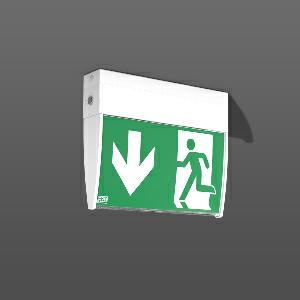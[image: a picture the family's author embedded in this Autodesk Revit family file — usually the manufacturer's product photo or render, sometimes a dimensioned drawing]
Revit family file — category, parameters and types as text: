
# Revit family: gsun_d_672219_002_1_04_1060
name_source: partatom
category: Lighting Fixtures
units: mm (PartAtom-declared; Revit-internal decimal feet)

## family parameters
Cut with Voids When Loaded = No
Host = Face
Light Source = No
Part Type = Normal
Room Calculation Point = No
Round Connector Dimension = Use Diameter
Shared = No

## types (1)
- GSUN D
    Apparent Load = 0 VA
    Default Elevation = 1800 mm
    Description = Series: GSUN D
Luminaire for escape route identification. Housing: extruded aluminium profile, powder-coated. 4 legends and 1 white lay in plastic sheet included. Universal mounting kit for ceiling and wall surface mounting. Electronic ballast included. Self-contained system with automatic self-test and feedback to the RZB monitoring system MULTIDIGIT. 
Colour: white
Length: 247 mm
Width: 45 mm
Height: 200 mm
Weight: 0.9 kg
Operating mode: maintained power mode
Viewing Distance: 24 m
Duration time: 3 h
Lamp: LED
Socket: without socket
Colour temperature: 4000K
System power: 4.7 W
Control gear: Regulated power supply
Protection class: I
Type of protection: IP 30
    Height = 200 mm  [stored 0.656168 ft]
    Lamp = 0 x
    Length = 247 mm
    Luminous efficacy = 0 lm/W
    Manufacturer = RZB
    ModVariant = No
    Model = 672219.002.1.04
    Mounting Place = Ceiling, Wall
    Mounting Type = Surface mounted
    Number of Poles = 1
    OnlyDefault = Yes
    Power Factor = 1
    Product Name = GSUN D
    Product group = Surface mounted ceiling and wall luminaires
    ProductGroupID = 305
    Protection Class = Protection class I
    Protection Degree = IP 30
    RLX_Detail_Level = 1
    RLX_Emergency_Light_Flux = 0 lm
    RLX_Emergency_Type = 0
    RLX_Emergency_Type_DB = No
    RlxData = <blob elided: 30085 chars, md5=b2e42442>
    Standby Power = 0 W
    System Light Flux = 0 lm
    System Power = 0 W
    Type Comments = Product without accessories
    Type Image = 671995.002.1.jpg
    URL = http://relux.com
    VarID = ---
    Voltage = 230 V
    Voltage Range = 220-240 V
    Weight = 0.00 kg
    Width = 45 mm

note: [stored X ft] marks values corroborated as IEEE doubles in the binary element streams (Revit-internal decimal feet)

## geometry (parser evidence)
native form markers: Blend x4, Sweep x10
no freeform markers — native parametric forms only
